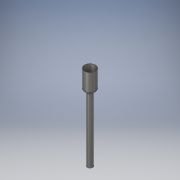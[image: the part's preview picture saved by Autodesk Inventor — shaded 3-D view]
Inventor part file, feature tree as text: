
AUTODESK INVENTOR PART (.ipt)
format: ipt  version: 2018 (Build 220112000, 112)  size: 135,680 bytes
history: native  units: in
note: dims shown in document units (in); Inventor stores cm internally (conversion verified against a paired STEP export)
features: extrude x3, sketch x3, fillet x2
ambient origin geometry x8: Origin, YZ Plane, XZ Plane, XY Plane, X Axis, Y Axis, Z Axis, Center Point
bodies: Solid1 (feature_tree)
feature tree (8):
  extrude  "Extrusion1"  Depth=0.96in
  extrude  "Extrusion2"  Depth=12.0in
  extrude  "Extrusion3"  Depth=12.0in TaperAngle=0.0deg
  fillet  "Fillet1"  Radius=2.0in
  fillet  "Fillet2"  Radius=0.05in
  sketch  "Sketch1"  dims[d0=0.9843in d1=0.96in]
  sketch  "Sketch2"  dims[d2=12.0in d3=0.0in d4=2.0in]
  sketch  "Sketch3"  dims[d5=1.95in d6=12.0in d7=0.0in d8=2.0in d9=0.05in d10=0.0in d11=0.31in d12=0.96in d13=0.31in]
